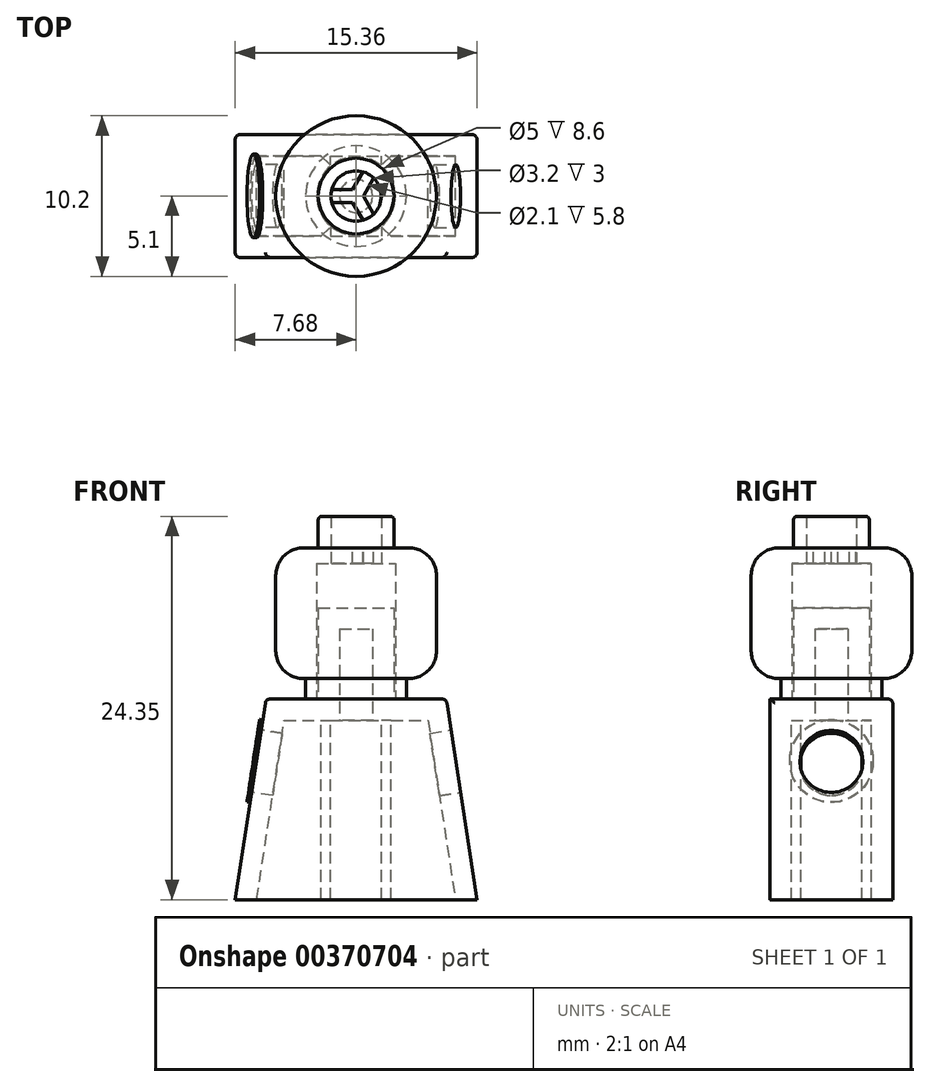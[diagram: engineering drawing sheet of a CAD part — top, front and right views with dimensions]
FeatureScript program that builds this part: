
annotation { "Feature Type Name" : "Feature", "Feature Type Description" : "" }
export const myFeature = defineFeature(function(context is Context, id is Id, definition is map)
    precondition{}
    {
        {
            var Q0;
            Q0=qCreatedBy(makeId("Front.planeOp"),FACE);
            var sketch = newSketch(context, id + "F0", { "sketchPlane" : qUnion([Q0])});
            skLineSegment(sketch, "E0", {"start": v(0, 0) * mm, "end": v(0, 11.6) * mm, "construction": true});
            skLineSegment(sketch, "E1", {"start": v(0, 0) * mm, "end": v(2.5, 0) * mm});
            skLineSegment(sketch, "E2", {"start": v(2.5, 0) * mm, "end": v(3.2, 0) * mm});
            skLineSegment(sketch, "E3", {"start": v(3.2, 0) * mm, "end": v(3.2, 1.3) * mm});
            skLineSegment(sketch, "E4", {"start": v(3.2, 1.3) * mm, "end": v(3.35, 1.3) * mm});
            skLineSegment(sketch, "E5", {"start": v(5.1, 3.05) * mm, "end": v(5.1, 7.85) * mm});
            skLineSegment(sketch, "E6", {"start": v(3.35, 9.6) * mm, "end": v(2.4, 9.6) * mm});
            skLineSegment(sketch, "E7", {"start": v(2.4, 9.6) * mm, "end": v(2.4, 11.4) * mm});
            skLineSegment(sketch, "E8", {"start": v(2.2, 11.6) * mm, "end": v(1.6, 11.6) * mm});
            skLineSegment(sketch, "E9", {"start": v(1.6, 11.6) * mm, "end": v(1.6, 9.6) * mm});
            skLineSegment(sketch, "E10", {"start": v(1.6, 9.6) * mm, "end": v(0, 9.6) * mm});
            skLineSegment(sketch, "E11", {"start": v(0, 9.6) * mm, "end": v(0, 8.6) * mm});
            skLineSegment(sketch, "E12", {"start": v(0, 8.6) * mm, "end": v(2.5, 8.6) * mm});
            skLineSegment(sketch, "E13", {"start": v(2.5, 8.6) * mm, "end": v(2.5, 0) * mm});
            skPoint(sketch, "E14.visualSharp", {"position": v(5.1, 9.6) * mm});
            skArc(sketch, "E14.filletArc", {"start": v(5.1, 7.85) * mm, "mid": v(4.59, 9.09) * mm, "end": v(3.35, 9.6) * mm});
            skPoint(sketch, "E15.visualSharp", {"position": v(5.1, 1.3) * mm});
            skArc(sketch, "E15.filletArc", {"start": v(3.35, 1.3) * mm, "mid": v(4.59, 1.81) * mm, "end": v(5.1, 3.05) * mm});
            skPoint(sketch, "E16.visualSharp", {"position": v(2.4, 11.6) * mm});
            skArc(sketch, "E16.filletArc", {"start": v(2.4, 11.4) * mm, "mid": v(2.34, 11.54) * mm, "end": v(2.2, 11.6) * mm});
            skSolve(sketch);
        }
        {
            var Q0;
            Q0=makeQuery(id+"F0.imprint","IMPRINT",FACE,{"disambiguationData":[TD([[makeQuery(id+"F0.imprint","IMPRINT",EDGE,{"derivedFrom":sQuery(id+"F0.wireOp",EDGE,"E2")}),1.0]])]});
            var Q1;
            Q1=sQuery(id+"F0.wireOp",EDGE,"E0");
            revolve(context, id + "F1", {"entities" : qUnion([Q0]), "axis" : qUnion([Q1]), "revolveType" : RevolveType.FULL});
        }
        {
            var Q0;
            Q0=makeQuery(id+"F1.opRevolve","SWEPT_FACE",FACE,{"disambiguationData":[OSD([sQuery(id+"F0.wireOp",EDGE,"E10")])]});
            var sketch = newSketch(context, id + "F2", { "sketchPlane" : qUnion([Q0])});
            skCircle(sketch, "E17", {"center": v(0, 0) * mm, "radius": 0.4 * mm});
            skLineSegment(sketch, "E18", {"start": v(0, 0) * mm, "end": v(0, 0.4) * mm, "construction": true});
            skLineSegment(sketch, "E19", {"start": v(0, 0.4) * mm, "end": v(0, -0.4) * mm, "construction": true});
            skLineSegment(sketch, "E20", {"start": v(0, -0.4) * mm, "end": v(-1.55, -0.4) * mm});
            skLineSegment(sketch, "E21", {"start": v(0, 0.4) * mm, "end": v(-1.55, 0.4) * mm});
            skLineSegment(sketch, "E22.1.0", {"start": v(-0.35, -0.2) * mm, "end": v(0.43, -1.54) * mm});
            skLineSegment(sketch, "E22.1.1", {"start": v(0.35, 0.2) * mm, "end": v(1.12, -1.14) * mm});
            skLineSegment(sketch, "E22.2.0", {"start": v(0.35, -0.2) * mm, "end": v(1.12, 1.14) * mm});
            skLineSegment(sketch, "E22.2.1", {"start": v(-0.35, 0.2) * mm, "end": v(0.43, 1.54) * mm});
            skSolve(sketch);
        }
        {
            var Q0;
            {var subQ0=sQuery(id+"F2.wireOp",EDGE,"E21");var subQ3=sQuery(id+"F2.wireOp",EDGE,"E22.2.1");var subQ4=makeQuery(id+"F2.imprint","INTERSECT",VERTEX,{"derivedFrom":[subQ0,subQ3]});Q0=makeQuery(id+"F2.imprint","IMPRINT",FACE,{"disambiguationData":[TD([[makeQuery(id+"F2.imprint","IMPRINT",EDGE,{"disambiguationData":[TD([[subQ4,-1.0]])],"derivedFrom":subQ0}),-1.0]])]});}
            var Q1;
            {var subQ0=sQuery(id+"F2.wireOp",EDGE,"E20");var subQ3=sQuery(id+"F2.wireOp",EDGE,"E22.1.0");var subQ4=makeQuery(id+"F2.imprint","INTERSECT",VERTEX,{"derivedFrom":[subQ0,subQ3]});Q1=makeQuery(id+"F2.imprint","IMPRINT",FACE,{"disambiguationData":[TD([[makeQuery(id+"F2.imprint","IMPRINT",EDGE,{"disambiguationData":[TD([[subQ4,-1.0]])],"derivedFrom":subQ0}),1.0]])]});}
            var Q2;
            {var subQ0=sQuery(id+"F2.wireOp",EDGE,"E22.1.1");var subQ3=sQuery(id+"F2.wireOp",EDGE,"E22.2.0");var subQ4=makeQuery(id+"F2.imprint","INTERSECT",VERTEX,{"derivedFrom":[subQ0,subQ3]});Q2=makeQuery(id+"F2.imprint","IMPRINT",FACE,{"disambiguationData":[TD([[makeQuery(id+"F2.imprint","IMPRINT",EDGE,{"disambiguationData":[TD([[subQ4,-1.0]])],"derivedFrom":subQ0}),1.0]])]});}
            extrude(context, id + "F3", {"entities" : qUnion([Q0, Q1, Q2]), "operationType" : NewBodyOperationType.REMOVE, "oppositeDirection" : true, "depth" : 5 * mm});
        }
        {
            var Q0;
            Q0=makeQuery(id+"F1.opRevolve","SWEPT_FACE",FACE,{"disambiguationData":[OSD([sQuery(id+"F0.wireOp",EDGE,"E2")])]});
            var sketch = newSketch(context, id + "F4", { "sketchPlane" : qUnion([Q0])});
            skCircle(sketch, "E23", {"center": v(0, 0) * mm, "radius": 2.4 * mm});
            skSolve(sketch);
        }
        {
            var Q0;
            Q0=makeQuery(id+"F4.imprint","IMPRINT",FACE,{"disambiguationData":[TD([[makeQuery(id+"F4.imprint","IMPRINT",EDGE,{"derivedFrom":sQuery(id+"F4.wireOp",EDGE,"E23")}),1.0]])]});
            extrude(context, id + "F5", {"entities" : qUnion([Q0]), "oppositeDirection" : true, "depth" : 5.8 * mm});
        }
        {
            var Q0;
            Q0=qCreatedBy(makeId("Front.planeOp"),FACE);
            var sketch = newSketch(context, id + "F6", { "sketchPlane" : qUnion([Q0])});
            skLineSegment(sketch, "E24", {"start": v(0, 0) * mm, "end": v(0, -12.75) * mm, "construction": true});
            skLineSegment(sketch, "E25", {"start": v(-5.72, 0) * mm, "end": v(5.72, 0) * mm});
            skLineSegment(sketch, "E26", {"start": v(5.72, 0) * mm, "end": v(7.68, -12.75) * mm});
            skLineSegment(sketch, "E27", {"start": v(7.68, -12.75) * mm, "end": v(-7.67, -12.75) * mm});
            skLineSegment(sketch, "E28", {"start": v(-7.68, -12.75) * mm, "end": v(-5.73, 0) * mm});
            skSolve(sketch);
        }
        {
            var Q0;
            Q0=makeQuery(id+"F6.imprint","IMPRINT",FACE,{"disambiguationData":[TD([[makeQuery(id+"F6.imprint","IMPRINT",EDGE,{"derivedFrom":sQuery(id+"F6.wireOp",EDGE,"E25")}),-1.0]])]});
            extrude(context, id + "F7", {"entities" : qUnion([Q0]), "operationType" : NewBodyOperationType.ADD, "endBound" : BoundingType.SYMMETRIC, "depth" : 7.8 * mm});
        }
        {
            var Q0;
            Q0=makeQuery(id+"F7.opExtrude","SWEPT_FACE",FACE,{"disambiguationData":[OSD([sQuery(id+"F6.wireOp",EDGE,"E27")])]});
            shell(context, id + "F8", {"entities" : qUnion([Q0]), "thickness" : 1.35 * mm});
        }
        {
            var Q0;
            Q0=makeQuery(id+"F8.opShell","OFFSET_FACE",FACE,{"disambiguationData":[OSD([sQuery(id+"F6.wireOp",EDGE,"E25")])]});
            var sketch = newSketch(context, id + "F9", { "sketchPlane" : qUnion([Q0])});
            skLineSegment(sketch, "E29", {"start": v(0, 2.55) * mm, "end": v(0, -2.55) * mm, "construction": true});
            skLineSegment(sketch, "E30", {"start": v(-1.63, 2.55) * mm, "end": v(-2.23, 2.55) * mm});
            skLineSegment(sketch, "E31", {"start": v(-2.23, 2.55) * mm, "end": v(-1.63, 1.95) * mm});
            skLineSegment(sketch, "E32", {"start": v(-1.63, 1.95) * mm, "end": v(-1.63, 2.55) * mm});
            skLineSegment(sketch, "E33", {"start": v(-1.63, 2.55) * mm, "end": v(0, 2.55) * mm});
            skLineSegment(sketch, "E34", {"start": v(-4.57, 0) * mm, "end": v(4.57, 0) * mm, "construction": true});
            skLineSegment(sketch, "E35.MirrorCS", {"start": v(1.62, 1.95) * mm, "end": v(1.62, 2.55) * mm});
            skLineSegment(sketch, "E36.MirrorCS", {"start": v(1.62, 2.55) * mm, "end": v(2.22, 2.55) * mm});
            skLineSegment(sketch, "E37.MirrorCS", {"start": v(2.22, 2.55) * mm, "end": v(1.62, 1.95) * mm});
            skLineSegment(sketch, "E38.MirrorCS", {"start": v(-1.62, -2.55) * mm, "end": v(-2.22, -2.55) * mm});
            skLineSegment(sketch, "E39.MirrorCS", {"start": v(1.62, -1.95) * mm, "end": v(1.62, -2.55) * mm});
            skLineSegment(sketch, "E40.MirrorCS", {"start": v(1.62, -2.55) * mm, "end": v(2.22, -2.55) * mm});
            skLineSegment(sketch, "E41.MirrorCS", {"start": v(-1.62, -2.55) * mm, "end": v(0, -2.55) * mm});
            skLineSegment(sketch, "E42.MirrorCS", {"start": v(-1.62, -1.95) * mm, "end": v(-1.62, -2.55) * mm});
            skLineSegment(sketch, "E43.MirrorCS", {"start": v(-2.22, -2.55) * mm, "end": v(-1.62, -1.95) * mm});
            skLineSegment(sketch, "E44.MirrorCS", {"start": v(0, -2.55) * mm, "end": v(0, 2.55) * mm, "construction": true});
            skLineSegment(sketch, "E45.MirrorCS", {"start": v(2.23, -2.55) * mm, "end": v(1.62, -1.95) * mm});
            skSolve(sketch);
        }
        {
            var Q0;
            Q0=makeQuery(id+"F7.opExtrude","SWEPT_FACE",FACE,{"disambiguationData":[OSD([sQuery(id+"F6.wireOp",EDGE,"E26")])]});
            var sketch = newSketch(context, id + "F10", { "sketchPlane" : qUnion([Q0])});
            skCircle(sketch, "E46", {"center": v(0, -4.87) * mm, "radius": 2 * mm});
            skPoint(sketch, "E46.centerSnap0", {"position": v(0, -0.87) * mm});
            skSolve(sketch);
        }
        {
            var Q0;
            Q0=makeQuery(id+"F9.imprint","IMPRINT",FACE,{"disambiguationData":[TD([[makeQuery(id+"F9.imprint","IMPRINT",EDGE,{"derivedFrom":sQuery(id+"F9.wireOp",EDGE,"E30")}),-1.0]])]});
            var Q1;
            Q1=makeQuery(id+"F9.imprint","IMPRINT",FACE,{"disambiguationData":[TD([[makeQuery(id+"F9.imprint","IMPRINT",EDGE,{"derivedFrom":sQuery(id+"F9.wireOp",EDGE,"E35.MirrorCS")}),-1.0]])]});
            var Q2;
            Q2=makeQuery(id+"F9.imprint","IMPRINT",FACE,{"disambiguationData":[TD([[makeQuery(id+"F9.imprint","IMPRINT",EDGE,{"derivedFrom":sQuery(id+"F9.wireOp",EDGE,"E39.MirrorCS")}),1.0]])]});
            var Q3;
            Q3=makeQuery(id+"F9.imprint","IMPRINT",FACE,{"disambiguationData":[TD([[makeQuery(id+"F9.imprint","IMPRINT",EDGE,{"derivedFrom":sQuery(id+"F9.wireOp",EDGE,"E38.MirrorCS")}),1.0]])]});
            var Q4;
            Q4=makeQuery(id+"F7.opExtrude","SWEPT_FACE",FACE,{"disambiguationData":[OSD([sQuery(id+"F6.wireOp",EDGE,"E27")])]});
            extrude(context, id + "F11", {"entities" : qUnion([Q0, Q1, Q2, Q3]), "operationType" : NewBodyOperationType.ADD, "endBound" : BoundingType.UP_TO_SURFACE, "endBoundEntityFace" : qUnion([Q4]), "depth" : 25 * mm});
        }
        {
            var Q0;
            Q0=makeQuery(id+"F7.opExtrude","SWEPT_FACE",FACE,{"disambiguationData":[OSD([sQuery(id+"F6.wireOp",EDGE,"E28")])]});
            var sketch = newSketch(context, id + "F12", { "sketchPlane" : qUnion([Q0])});
            skCircle(sketch, "E47", {"center": v(0, -4.87) * mm, "radius": 2 * mm});
            skPoint(sketch, "E47.centerSnap0", {"position": v(0, -0.87) * mm});
            skSolve(sketch);
        }
        {
            var Q0;
            Q0=makeQuery(id+"F10.imprint","IMPRINT",FACE,{"disambiguationData":[TD([[makeQuery(id+"F10.imprint","IMPRINT",EDGE,{"derivedFrom":sQuery(id+"F10.wireOp",EDGE,"E46")}),1.0]])]});
            extrude(context, id + "F13", {"entities" : qUnion([Q0]), "operationType" : NewBodyOperationType.REMOVE, "oppositeDirection" : true, "depth" : 1.35 * mm});
        }
        {
            var Q0;
            Q0=makeQuery(id+"F12.imprint","IMPRINT",FACE,{"disambiguationData":[TD([[makeQuery(id+"F12.imprint","IMPRINT",EDGE,{"derivedFrom":sQuery(id+"F12.wireOp",EDGE,"E47")}),1.0]])]});
            extrude(context, id + "F14", {"entities" : qUnion([Q0]), "operationType" : NewBodyOperationType.REMOVE, "oppositeDirection" : true, "depth" : 1.35 * mm});
        }
        {
            var Q0;
            Q0=makeQuery(id+"F7.opExtrude","CAP_EDGE",EDGE,{"disambiguationData":[OSD([sQuery(id+"F6.wireOp",EDGE,"E28")])],"isStart":false});
            var Q1;
            Q1=makeQuery(id+"F7.opExtrude","SWEPT_EDGE",EDGE,{"disambiguationData":[OSD([sQuery(id+"F6.wireOp",EDGE,"E25"),sQuery(id+"F6.wireOp",EDGE,"E28")])]});
            var Q2;
            Q2=makeQuery(id+"F7.opExtrude","CAP_EDGE",EDGE,{"disambiguationData":[OSD([sQuery(id+"F6.wireOp",EDGE,"E28")])],"isStart":true});
            var Q3;
            Q3=makeQuery(id+"F7.opExtrude","CAP_EDGE",EDGE,{"disambiguationData":[OSD([sQuery(id+"F6.wireOp",EDGE,"E25")])],"isStart":true});
            var Q4;
            Q4=makeQuery(id+"F7.opExtrude","CAP_EDGE",EDGE,{"disambiguationData":[OSD([sQuery(id+"F6.wireOp",EDGE,"E26")])],"isStart":true});
            var Q5;
            Q5=makeQuery(id+"F7.opExtrude","SWEPT_EDGE",EDGE,{"disambiguationData":[OSD([sQuery(id+"F6.wireOp",EDGE,"E25"),sQuery(id+"F6.wireOp",EDGE,"E26")])]});
            var Q6;
            Q6=makeQuery(id+"F7.opExtrude","CAP_EDGE",EDGE,{"disambiguationData":[OSD([sQuery(id+"F6.wireOp",EDGE,"E26")])],"isStart":false});
            fillet(context, id + "F15", {"entities" : qUnion([Q0, Q1, Q2, Q3, Q4, Q5, Q6]), "radius" : 0.3 * mm, "tangentPropagation" : true, "allowEdgeOverflow" : false});
        }
        {
            var Q0;
            Q0=makeQuery(id+"F7.opExtrude","SWEPT_FACE",FACE,{"disambiguationData":[OSD([sQuery(id+"F6.wireOp",EDGE,"E28")])]});
            var sketch = newSketch(context, id + "F16", { "sketchPlane" : qUnion([Q0])});
            skCircle(sketch, "E48", {"center": v(0, -4.87) * mm, "radius": 2.65 * mm});
            skSolve(sketch);
        }
        {
            var Q0;
            Q0 = qSketchRegion(id + "F16", true);
            extrude(context, id + "F17", {"entities" : qUnion([Q0]), "depth" : 0.2 * mm});
        }
    });
